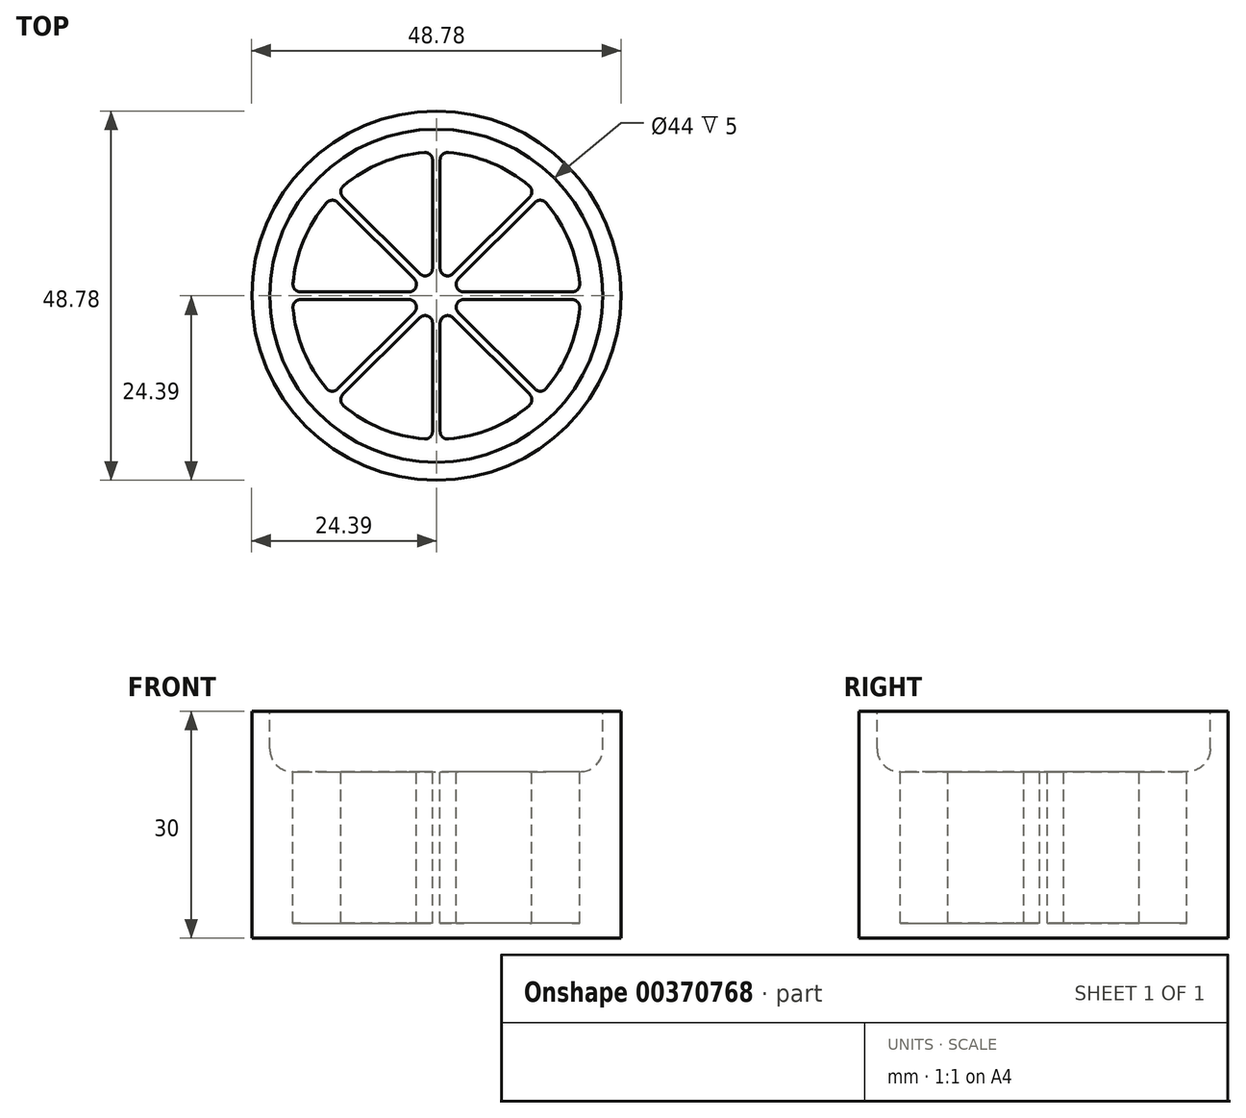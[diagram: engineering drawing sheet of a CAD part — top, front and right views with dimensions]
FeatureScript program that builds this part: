
annotation { "Feature Type Name" : "Feature", "Feature Type Description" : "" }
export const myFeature = defineFeature(function(context is Context, id is Id, definition is map)
    precondition{}
    {
        {
            var Q0;
            Q0=qCreatedBy(makeId("Top.planeOp"),FACE);
            var sketch = newSketch(context, id + "F0", { "sketchPlane" : qUnion([Q0])});
            skCircle(sketch, "E0", {"center": v(0, 0) * mm, "radius": 24.39 * mm});
            skSolve(sketch);
        }
        {
            var Q0;
            Q0=makeQuery(id+"F0.imprint","IMPRINT",FACE,{"disambiguationData":[TD([[makeQuery(id+"F0.imprint","IMPRINT",EDGE,{"derivedFrom":sQuery(id+"F0.wireOp",EDGE,"E0")}),1.0]])]});
            extrude(context, id + "F1", {"entities" : qUnion([Q0]), "depth" : 30 * mm});
        }
        {
            var Q0;
            Q0=makeQuery(id+"F1.opExtrude","CAP_FACE",FACE,{"disambiguationData":[OSD([sQuery(id+"F0.wireOp",EDGE,"E0")])],"isStart":false});
            var sketch = newSketch(context, id + "F2", { "sketchPlane" : qUnion([Q0])});
            skCircle(sketch, "E1", {"center": v(0, 0) * mm, "radius": 22 * mm});
            skSolve(sketch);
        }
        {
            var Q0;
            Q0=makeQuery(id+"F2.imprint","IMPRINT",FACE,{"disambiguationData":[TD([[makeQuery(id+"F2.imprint","IMPRINT",EDGE,{"derivedFrom":sQuery(id+"F2.wireOp",EDGE,"E1")}),1.0]])]});
            extrude(context, id + "F3", {"entities" : qUnion([Q0]), "operationType" : NewBodyOperationType.REMOVE, "oppositeDirection" : true, "depth" : 8 * mm});
        }
        {
            var Q0;
            Q0=makeQuery(id+"F3.boolean.opBoolean","COPY",EDGE,{"derivedFrom":makeQuery(id+"F3.opExtrude","CAP_EDGE",EDGE,{"disambiguationData":[OSD([sQuery(id+"F2.wireOp",EDGE,"E1")])],"isStart":false})});
            fillet(context, id + "F4", {"entities" : qUnion([Q0]), "radius" : 3 * mm, "tangentPropagation" : true, "allowEdgeOverflow" : false});
        }
        {
            var Q0;
            Q0=makeQuery(id+"F3.boolean.opBoolean","COPY",FACE,{"derivedFrom":makeQuery(id+"F3.opExtrude","CAP_FACE",FACE,{"disambiguationData":[OSD([sQuery(id+"F2.wireOp",EDGE,"E1")])],"isStart":false})});
            var sketch = newSketch(context, id + "F5", { "sketchPlane" : qUnion([Q0])});
            skLineSegment(sketch, "E2.bottom", {"start": v(-19, -0.5) * mm, "end": v(-1.2, -0.5) * mm});
            skLineSegment(sketch, "E2.top", {"start": v(-19, 0.5) * mm, "end": v(-1.2, 0.5) * mm});
            skLineSegment(sketch, "E3.1.0", {"start": v(-13.08, -13.78) * mm, "end": v(-0.5, -1.2) * mm});
            skLineSegment(sketch, "E3.1.1", {"start": v(-13.78, -13.08) * mm, "end": v(-1.2, -0.5) * mm});
            skLineSegment(sketch, "E3.2.0", {"start": v(0.5, -19) * mm, "end": v(0.5, -1.2) * mm});
            skLineSegment(sketch, "E3.2.1", {"start": v(-0.5, -19) * mm, "end": v(-0.5, -1.2) * mm});
            skLineSegment(sketch, "E3.3.0", {"start": v(13.78, -13.08) * mm, "end": v(1.2, -0.5) * mm});
            skLineSegment(sketch, "E3.3.1", {"start": v(13.08, -13.78) * mm, "end": v(0.5, -1.2) * mm});
            skLineSegment(sketch, "E3.4.0", {"start": v(19, 0.5) * mm, "end": v(1.2, 0.5) * mm});
            skLineSegment(sketch, "E3.4.1", {"start": v(19, -0.5) * mm, "end": v(1.2, -0.5) * mm});
            skLineSegment(sketch, "E3.5.0", {"start": v(13.08, 13.78) * mm, "end": v(0.5, 1.2) * mm});
            skLineSegment(sketch, "E3.5.1", {"start": v(13.78, 13.08) * mm, "end": v(1.2, 0.5) * mm});
            skLineSegment(sketch, "E3.6.0", {"start": v(-0.5, 19) * mm, "end": v(-0.5, 1.2) * mm});
            skLineSegment(sketch, "E3.6.1", {"start": v(0.5, 19) * mm, "end": v(0.5, 1.2) * mm});
            skLineSegment(sketch, "E3.7.0", {"start": v(-13.78, 13.08) * mm, "end": v(-1.2, 0.5) * mm});
            skLineSegment(sketch, "E3.7.1", {"start": v(-13.08, 13.78) * mm, "end": v(-0.5, 1.2) * mm});
            skArc(sketch, "E4", {"start": v(-13.78, 13.08) * mm, "mid": v(-17.55, 7.27) * mm, "end": v(-19, 0.5) * mm});
            skArc(sketch, "E5.trimOffspring", {"start": v(-19, -0.5) * mm, "mid": v(-17.55, -7.27) * mm, "end": v(-13.78, -13.08) * mm});
            skArc(sketch, "E6.trimOffspring", {"start": v(-13.08, -13.78) * mm, "mid": v(-7.27, -17.55) * mm, "end": v(-0.5, -19) * mm});
            skArc(sketch, "E7.trimOffspring", {"start": v(0.5, -19) * mm, "mid": v(7.27, -17.55) * mm, "end": v(13.08, -13.78) * mm});
            skArc(sketch, "E8.trimOffspring", {"start": v(13.78, -13.08) * mm, "mid": v(17.55, -7.27) * mm, "end": v(19, -0.5) * mm});
            skArc(sketch, "E9.trimOffspring", {"start": v(19, 0.5) * mm, "mid": v(17.55, 7.27) * mm, "end": v(13.78, 13.08) * mm});
            skArc(sketch, "E10.trimOffspring", {"start": v(13.08, 13.78) * mm, "mid": v(7.27, 17.55) * mm, "end": v(0.5, 19) * mm});
            skArc(sketch, "E11.trimOffspring", {"start": v(-0.5, 19) * mm, "mid": v(-7.27, 17.55) * mm, "end": v(-13.08, 13.78) * mm});
            skSolve(sketch);
        }
        {
            var Q0;
            Q0 = qSketchRegion(id + "F5", true);
            extrude(context, id + "F6", {"entities" : qUnion([Q0]), "operationType" : NewBodyOperationType.REMOVE, "oppositeDirection" : true, "depth" : 20 * mm});
        }
        {
            var Q0;
            Q0=makeQuery(id+"F6.boolean.opBoolean","COPY",EDGE,{"derivedFrom":makeQuery(id+"F6.opExtrude","SWEPT_EDGE",EDGE,{"disambiguationData":[OSD([sQuery(id+"F2.wireOp",EDGE,"E1"),sQuery(id+"F5.wireOp",EDGE,"E2.top"),sQuery(id+"F5.wireOp",EDGE,"E4")])]})});
            var Q1;
            Q1=makeQuery(id+"F6.boolean.opBoolean","COPY",EDGE,{"derivedFrom":makeQuery(id+"F6.opExtrude","SWEPT_EDGE",EDGE,{"disambiguationData":[OSD([sQuery(id+"F2.wireOp",EDGE,"E1"),sQuery(id+"F5.wireOp",EDGE,"E2.bottom"),sQuery(id+"F5.wireOp",EDGE,"E5.trimOffspring")])]})});
            var Q2;
            Q2=makeQuery(id+"F6.boolean.opBoolean","COPY",EDGE,{"derivedFrom":makeQuery(id+"F6.opExtrude","SWEPT_EDGE",EDGE,{"disambiguationData":[OSD([sQuery(id+"F2.wireOp",EDGE,"E1"),sQuery(id+"F5.wireOp",EDGE,"E3.7.1"),sQuery(id+"F5.wireOp",EDGE,"E11.trimOffspring")])]})});
            var Q3;
            Q3=makeQuery(id+"F6.boolean.opBoolean","COPY",EDGE,{"derivedFrom":makeQuery(id+"F6.opExtrude","SWEPT_EDGE",EDGE,{"disambiguationData":[OSD([sQuery(id+"F2.wireOp",EDGE,"E1"),sQuery(id+"F5.wireOp",EDGE,"E3.7.0"),sQuery(id+"F5.wireOp",EDGE,"E4")])]})});
            var Q4;
            Q4=makeQuery(id+"F6.boolean.opBoolean","COPY",EDGE,{"derivedFrom":makeQuery(id+"F6.opExtrude","SWEPT_EDGE",EDGE,{"disambiguationData":[OSD([sQuery(id+"F2.wireOp",EDGE,"E1"),sQuery(id+"F5.wireOp",EDGE,"E3.6.1"),sQuery(id+"F5.wireOp",EDGE,"E10.trimOffspring")])]})});
            var Q5;
            Q5=makeQuery(id+"F6.boolean.opBoolean","COPY",EDGE,{"derivedFrom":makeQuery(id+"F6.opExtrude","SWEPT_EDGE",EDGE,{"disambiguationData":[OSD([sQuery(id+"F2.wireOp",EDGE,"E1"),sQuery(id+"F5.wireOp",EDGE,"E3.6.0"),sQuery(id+"F5.wireOp",EDGE,"E11.trimOffspring")])]})});
            var Q6;
            Q6=makeQuery(id+"F6.boolean.opBoolean","COPY",EDGE,{"derivedFrom":makeQuery(id+"F6.opExtrude","SWEPT_EDGE",EDGE,{"disambiguationData":[OSD([sQuery(id+"F2.wireOp",EDGE,"E1"),sQuery(id+"F5.wireOp",EDGE,"E3.5.0"),sQuery(id+"F5.wireOp",EDGE,"E10.trimOffspring")])]})});
            var Q7;
            Q7=makeQuery(id+"F6.boolean.opBoolean","COPY",EDGE,{"derivedFrom":makeQuery(id+"F6.opExtrude","SWEPT_EDGE",EDGE,{"disambiguationData":[OSD([sQuery(id+"F2.wireOp",EDGE,"E1"),sQuery(id+"F5.wireOp",EDGE,"E3.5.1"),sQuery(id+"F5.wireOp",EDGE,"E9.trimOffspring")])]})});
            var Q8;
            Q8=makeQuery(id+"F6.boolean.opBoolean","COPY",EDGE,{"derivedFrom":makeQuery(id+"F6.opExtrude","SWEPT_EDGE",EDGE,{"disambiguationData":[OSD([sQuery(id+"F2.wireOp",EDGE,"E1"),sQuery(id+"F5.wireOp",EDGE,"E3.4.0"),sQuery(id+"F5.wireOp",EDGE,"E9.trimOffspring")])]})});
            var Q9;
            Q9=makeQuery(id+"F6.boolean.opBoolean","COPY",EDGE,{"derivedFrom":makeQuery(id+"F6.opExtrude","SWEPT_EDGE",EDGE,{"disambiguationData":[OSD([sQuery(id+"F2.wireOp",EDGE,"E1"),sQuery(id+"F5.wireOp",EDGE,"E3.4.1"),sQuery(id+"F5.wireOp",EDGE,"E8.trimOffspring")])]})});
            var Q10;
            Q10=makeQuery(id+"F6.boolean.opBoolean","COPY",EDGE,{"derivedFrom":makeQuery(id+"F6.opExtrude","SWEPT_EDGE",EDGE,{"disambiguationData":[OSD([sQuery(id+"F2.wireOp",EDGE,"E1"),sQuery(id+"F5.wireOp",EDGE,"E3.3.1"),sQuery(id+"F5.wireOp",EDGE,"E7.trimOffspring")])]})});
            var Q11;
            Q11=makeQuery(id+"F6.boolean.opBoolean","COPY",EDGE,{"derivedFrom":makeQuery(id+"F6.opExtrude","SWEPT_EDGE",EDGE,{"disambiguationData":[OSD([sQuery(id+"F2.wireOp",EDGE,"E1"),sQuery(id+"F5.wireOp",EDGE,"E3.3.0"),sQuery(id+"F5.wireOp",EDGE,"E8.trimOffspring")])]})});
            var Q12;
            Q12=makeQuery(id+"F6.boolean.opBoolean","COPY",EDGE,{"derivedFrom":makeQuery(id+"F6.opExtrude","SWEPT_EDGE",EDGE,{"disambiguationData":[OSD([sQuery(id+"F2.wireOp",EDGE,"E1"),sQuery(id+"F5.wireOp",EDGE,"E3.2.0"),sQuery(id+"F5.wireOp",EDGE,"E7.trimOffspring")])]})});
            var Q13;
            Q13=makeQuery(id+"F6.boolean.opBoolean","COPY",EDGE,{"derivedFrom":makeQuery(id+"F6.opExtrude","SWEPT_EDGE",EDGE,{"disambiguationData":[OSD([sQuery(id+"F2.wireOp",EDGE,"E1"),sQuery(id+"F5.wireOp",EDGE,"E3.2.1"),sQuery(id+"F5.wireOp",EDGE,"E6.trimOffspring")])]})});
            var Q14;
            Q14=makeQuery(id+"F6.boolean.opBoolean","COPY",EDGE,{"derivedFrom":makeQuery(id+"F6.opExtrude","SWEPT_EDGE",EDGE,{"disambiguationData":[OSD([sQuery(id+"F2.wireOp",EDGE,"E1"),sQuery(id+"F5.wireOp",EDGE,"E3.1.0"),sQuery(id+"F5.wireOp",EDGE,"E6.trimOffspring")])]})});
            var Q15;
            Q15=makeQuery(id+"F6.boolean.opBoolean","COPY",EDGE,{"derivedFrom":makeQuery(id+"F6.opExtrude","SWEPT_EDGE",EDGE,{"disambiguationData":[OSD([sQuery(id+"F2.wireOp",EDGE,"E1"),sQuery(id+"F5.wireOp",EDGE,"E3.1.1"),sQuery(id+"F5.wireOp",EDGE,"E5.trimOffspring")])]})});
            var Q16;
            Q16=makeQuery(id+"F6.boolean.opBoolean","COPY",EDGE,{"derivedFrom":makeQuery(id+"F6.opExtrude","SWEPT_EDGE",EDGE,{"disambiguationData":[OSD([sQuery(id+"F5.wireOp",EDGE,"E3.1.0"),sQuery(id+"F5.wireOp",EDGE,"E3.2.1")])]})});
            var Q17;
            Q17=makeQuery(id+"F6.boolean.opBoolean","COPY",EDGE,{"derivedFrom":makeQuery(id+"F6.opExtrude","SWEPT_EDGE",EDGE,{"disambiguationData":[OSD([sQuery(id+"F5.wireOp",EDGE,"E2.bottom"),sQuery(id+"F5.wireOp",EDGE,"E3.1.1")])]})});
            var Q18;
            Q18=makeQuery(id+"F6.boolean.opBoolean","COPY",EDGE,{"derivedFrom":makeQuery(id+"F6.opExtrude","SWEPT_EDGE",EDGE,{"disambiguationData":[OSD([sQuery(id+"F5.wireOp",EDGE,"E2.top"),sQuery(id+"F5.wireOp",EDGE,"E3.7.0")])]})});
            var Q19;
            Q19=makeQuery(id+"F6.boolean.opBoolean","COPY",EDGE,{"derivedFrom":makeQuery(id+"F6.opExtrude","SWEPT_EDGE",EDGE,{"disambiguationData":[OSD([sQuery(id+"F5.wireOp",EDGE,"E3.6.0"),sQuery(id+"F5.wireOp",EDGE,"E3.7.1")])]})});
            var Q20;
            Q20=makeQuery(id+"F6.boolean.opBoolean","COPY",EDGE,{"derivedFrom":makeQuery(id+"F6.opExtrude","SWEPT_EDGE",EDGE,{"disambiguationData":[OSD([sQuery(id+"F5.wireOp",EDGE,"E3.5.0"),sQuery(id+"F5.wireOp",EDGE,"E3.6.1")])]})});
            var Q21;
            Q21=makeQuery(id+"F6.boolean.opBoolean","COPY",EDGE,{"derivedFrom":makeQuery(id+"F6.opExtrude","SWEPT_EDGE",EDGE,{"disambiguationData":[OSD([sQuery(id+"F5.wireOp",EDGE,"E3.4.0"),sQuery(id+"F5.wireOp",EDGE,"E3.5.1")])]})});
            var Q22;
            Q22=makeQuery(id+"F6.boolean.opBoolean","COPY",EDGE,{"derivedFrom":makeQuery(id+"F6.opExtrude","SWEPT_EDGE",EDGE,{"disambiguationData":[OSD([sQuery(id+"F5.wireOp",EDGE,"E3.3.0"),sQuery(id+"F5.wireOp",EDGE,"E3.4.1")])]})});
            var Q23;
            Q23=makeQuery(id+"F6.boolean.opBoolean","COPY",EDGE,{"derivedFrom":makeQuery(id+"F6.opExtrude","SWEPT_EDGE",EDGE,{"disambiguationData":[OSD([sQuery(id+"F5.wireOp",EDGE,"E3.2.0"),sQuery(id+"F5.wireOp",EDGE,"E3.3.1")])]})});
            fillet(context, id + "F7", {"entities" : qUnion([Q0, Q1, Q2, Q3, Q4, Q5, Q6, Q7, Q8, Q9, Q10, Q11, Q12, Q13, Q14, Q15, Q16, Q17, Q18, Q19, Q20, Q21, Q22, Q23]), "radius" : 1 * mm, "tangentPropagation" : true, "allowEdgeOverflow" : false});
        }
    });
